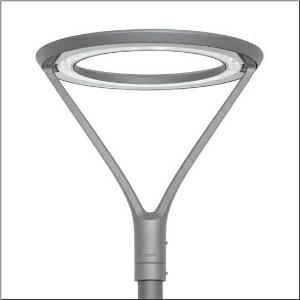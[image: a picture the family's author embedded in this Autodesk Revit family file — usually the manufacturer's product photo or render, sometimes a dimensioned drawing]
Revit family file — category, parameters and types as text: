
# Revit family: dl_r__20_led___st1_2a_5xa512832a008_fd59
name_source: partatom
category: Lighting Fixtures
units: mm (PartAtom-declared; Revit-internal decimal feet)

## family parameters
Cut with Voids When Loaded = No
Host = Face
Light Source = No
Part Type = Normal
Room Calculation Point = No
Round Connector Dimension = Use Diameter
Shared = No

## types (1)
- --- (1 x LED, 3010 lm, 33.7 W, 2200K)
    Apparent Load = 34 VA
    CIE Flux Codes = 31 69 96 100 100
    Color Rendering = 70
    Color Temperature = 2200K
    Default Elevation = 1800 mm
    Description = DL® 20 LED, mast luminaire, primary light control with reflector, highly specular, primary optical cover: cover, of toughened safety glass of clear glass with excellent transmission level, light distribution: ST1.2a, light emission: direct distribution, primary light characteristic: asymmetric, installation type: post-top, LED, High Power LED, rated luminous flux: 3.020lm, luminous efficacy: 85lm/W, light colour: 722, colour temperature: 2200K, control gear: ECG Plus, control: flexible luminous flux parameterisation, time-dependent luminous flux control, constant luminous flux control, digital communication interface, power reduction, overheat protection, electronic power reduction, mains connection: 220..240V, 50/60Hz, connection cable pre-assembled, cable length: 5m, start of lifetime: 36W, end of lifetime: 36W, reduction: 17W, luminaire housing, upper part, of cast aluminium, powder-coated, Siteco® metallic grey (DB 702S), diameter: 690mm, height: 690mm, spigot size: 76mm (post-top), luminaire housing, of cast aluminium, powder-coated, Siteco® metallic grey (DB 702S), protection rating (complete): IP66, insulation class (complete): insulation class II (safety insulation), certification: CE, ENEC, VDE, impact resistance: IK08, permissible operating ambient temperature: -25..+35°C, standard-compliant lighting for roads and squares, packaging unit: 1 piece

Light Distribution: ST1.2a
    Height = 690 mm
    Lamp = 1 x LED
    Lamp Light Flux = 3010 lm
    Lamp Power = 33.7 W
    Lamp count = 1
    Length = 690 mm
    Luminous efficacy = 89 lm/W
    Manufacturer = Siteco
    ModVariant = No
    Model = 5XA512832A008
    Number of Poles = 1
    OnlyDefault = Yes
    Power Factor = 1
    Product Name = DL® 20 LED | ST1.2a
    Product group = mast luminaire | pylon top
    ProductGroupID = 6100
    Protection Class = Protection class II
    Protection Degree = IP 66
    RLX_Detail_Level = 1
    RlxData = <blob elided: 206705 chars, md5=d576d39f>
    Socket = socket
    Standby Power = 0 W
    System Light Flux = 3010 lm
    System Power = 34 W
    Type Comments = factory setting: luminous flux: 100 % | dim-lin: 254 | 455 mA
    Type Image = l_1006001.jpg
    URL = http://relux.com
    VarID = @adj_118347
    Voltage = 0 V
    Weight = 0.00 kg
    Width = 0 mm  [stored 0 ft]

note: [stored X ft] marks values corroborated as IEEE doubles in the binary element streams (Revit-internal decimal feet)

## geometry (parser evidence)
native form markers: Blend x4, Sweep x10
no freeform markers — native parametric forms only
